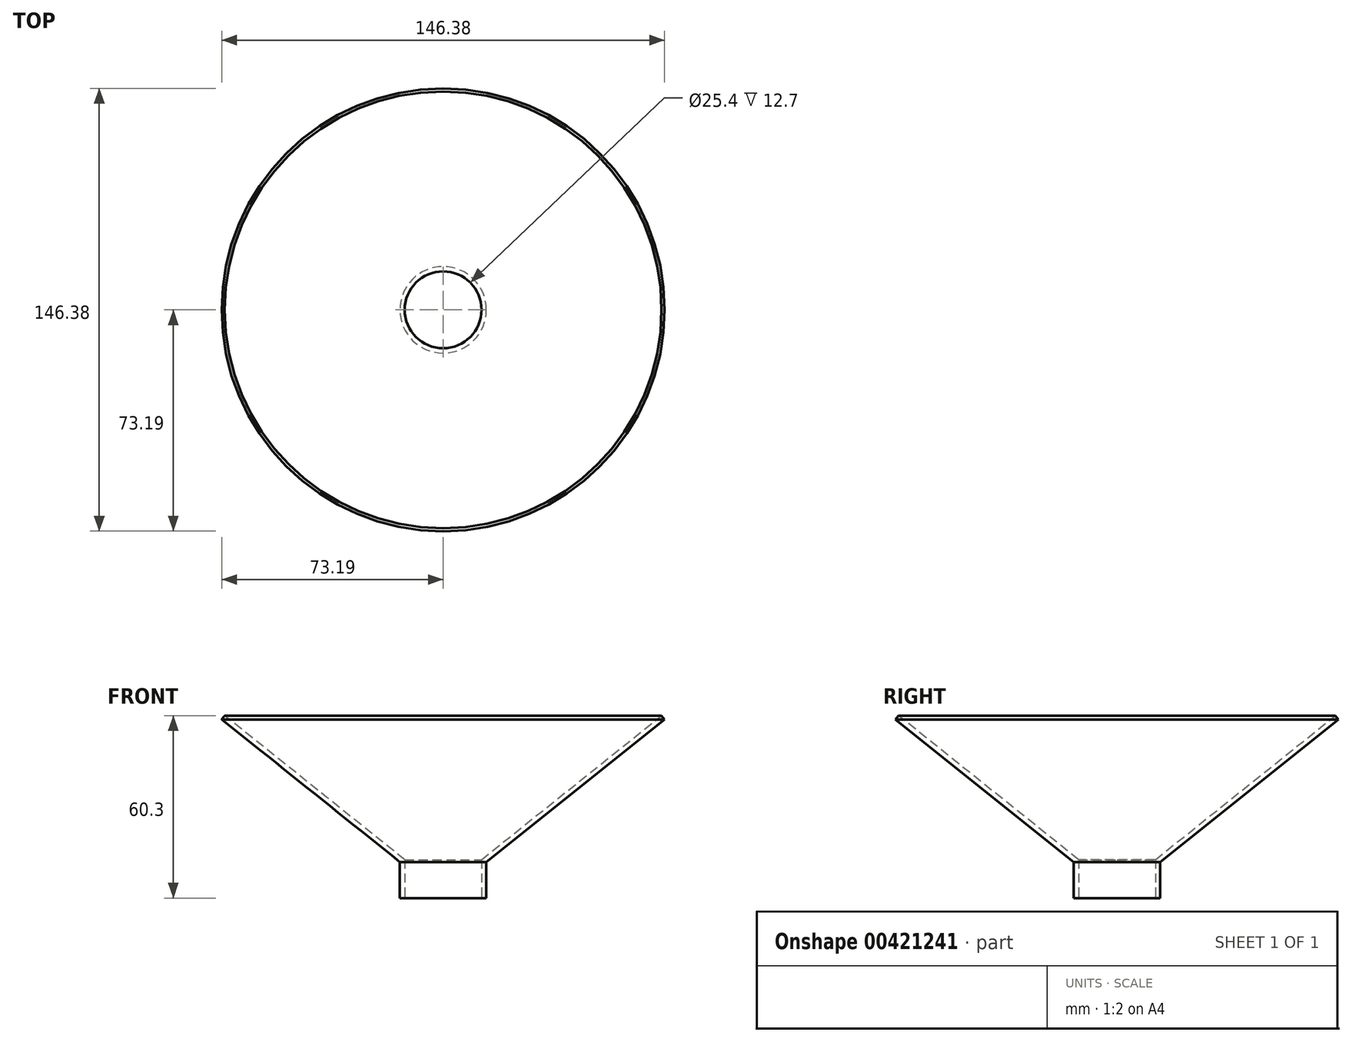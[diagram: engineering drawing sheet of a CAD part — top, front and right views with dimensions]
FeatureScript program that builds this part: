
annotation { "Feature Type Name" : "Feature", "Feature Type Description" : "" }
export const myFeature = defineFeature(function(context is Context, id is Id, definition is map)
    precondition{}
    {
        {
            var Q0;
            Q0=qCreatedBy(makeId("Front.planeOp"),FACE);
            var sketch = newSketch(context, id + "F0", { "sketchPlane" : qUnion([Q0])});
            skLineSegment(sketch, "E0", {"start": v(-12.7, 0) * mm, "end": v(-12.7, 12.7) * mm});
            skLineSegment(sketch, "E1", {"start": v(-12.7, 12.7) * mm, "end": v(-72.2, 60.3) * mm});
            skLineSegment(sketch, "E2", {"start": v(-72.2, 60.3) * mm, "end": v(-73.2, 59.06) * mm});
            skLineSegment(sketch, "E3", {"start": v(-12.7, 0) * mm, "end": v(-14.29, 0) * mm});
            skLineSegment(sketch, "E4", {"start": v(-73.2, 59.06) * mm, "end": v(-14.29, 11.94) * mm});
            skLineSegment(sketch, "E5", {"start": v(-14.29, 0) * mm, "end": v(-14.29, 11.94) * mm});
            skLineSegment(sketch, "E6", {"start": v(0, 0) * mm, "end": v(0, 44.48) * mm});
            skSolve(sketch);
        }
        {
            var Q0;
            Q0=makeQuery(id+"F0.imprint","IMPRINT",FACE,{"disambiguationData":[TD([[makeQuery(id+"F0.imprint","IMPRINT",EDGE,{"derivedFrom":sQuery(id+"F0.wireOp",EDGE,"E0")}),1.0]])]});
            var Q1;
            Q1=sQuery(id+"F0.wireOp",EDGE,"E6");
            revolve(context, id + "F1", {"entities" : qUnion([Q0]), "axis" : qUnion([Q1]), "revolveType" : RevolveType.FULL});
        }
    });
